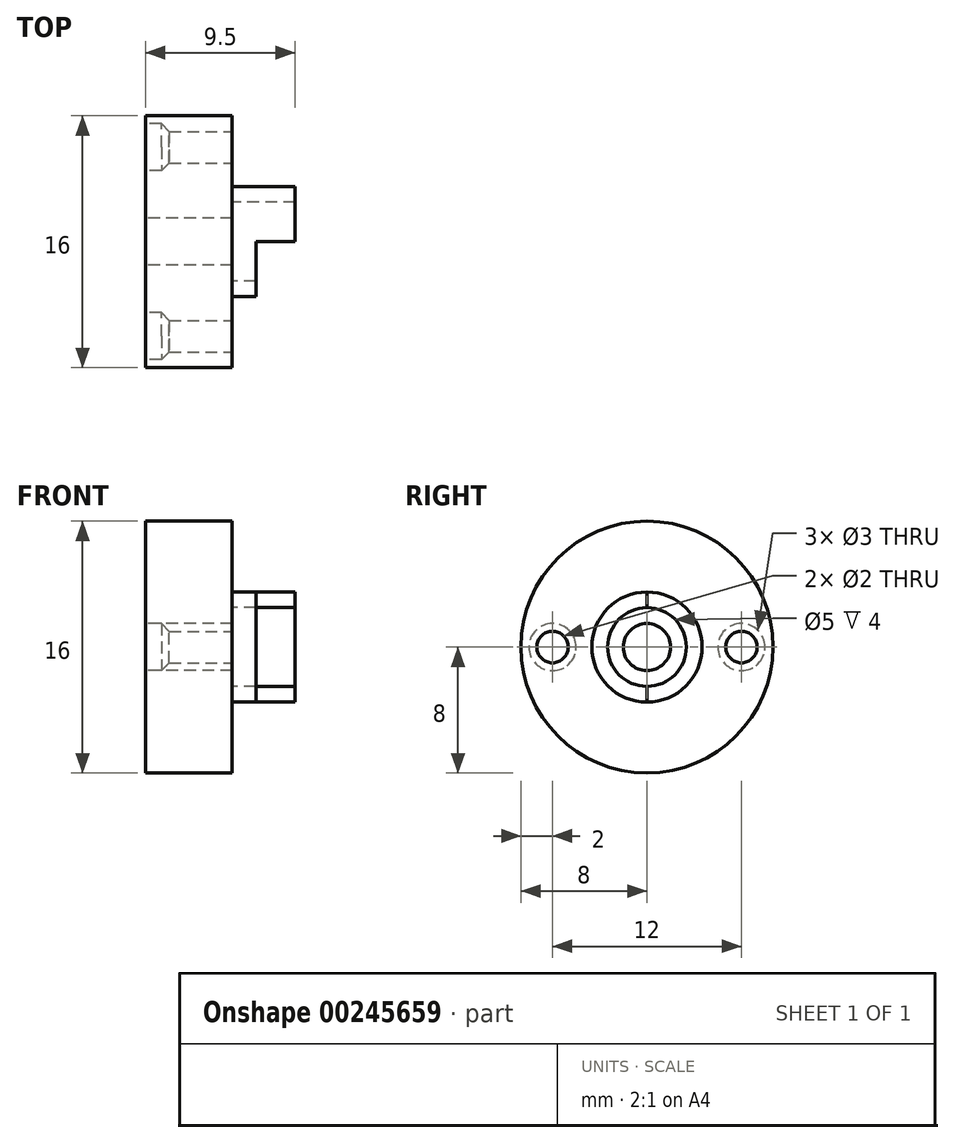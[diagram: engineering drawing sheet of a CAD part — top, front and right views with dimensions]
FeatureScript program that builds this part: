
annotation { "Feature Type Name" : "Feature", "Feature Type Description" : "" }
export const myFeature = defineFeature(function(context is Context, id is Id, definition is map)
    precondition{}
    {
        {
            var Q0;
            Q0=qCreatedBy(makeId("Right.planeOp"),FACE);
            var sketch = newSketch(context, id + "F0", { "sketchPlane" : qUnion([Q0])});
            skCircle(sketch, "E0", {"center": v(0, 0) * mm, "radius": 8 * mm});
            skSolve(sketch);
        }
        {
            var Q0;
            Q0=makeQuery(id+"F0.imprint","IMPRINT",FACE,{"disambiguationData":[TD([[makeQuery(id+"F0.imprint","IMPRINT",EDGE,{"derivedFrom":sQuery(id+"F0.wireOp",EDGE,"E0")}),1.0]])]});
            extrude(context, id + "F1", {"entities" : qUnion([Q0]), "depth" : 5.5 * mm});
        }
        {
            var Q0;
            Q0=makeQuery(id+"F1.opExtrude","CAP_FACE",FACE,{"disambiguationData":[OSD([sQuery(id+"F0.wireOp",EDGE,"E0")])],"isStart":false});
            var sketch = newSketch(context, id + "F2", { "sketchPlane" : qUnion([Q0])});
            skCircle(sketch, "E1", {"center": v(0, 0) * mm, "radius": 3.5 * mm});
            skSolve(sketch);
        }
        {
            var Q0;
            Q0=makeQuery(id+"F2.imprint","IMPRINT",FACE,{"disambiguationData":[TD([[makeQuery(id+"F2.imprint","IMPRINT",EDGE,{"derivedFrom":sQuery(id+"F2.wireOp",EDGE,"E1")}),1.0]])]});
            extrude(context, id + "F3", {"entities" : qUnion([Q0]), "operationType" : NewBodyOperationType.ADD, "depth" : 1.5 * mm});
        }
        {
            var Q0;
            Q0=makeQuery(id+"F3.opExtrude","CAP_FACE",FACE,{"disambiguationData":[OSD([sQuery(id+"F2.wireOp",EDGE,"E1")])],"isStart":false});
            var sketch = newSketch(context, id + "F4", { "sketchPlane" : qUnion([Q0])});
            skArc(sketch, "E2", {"start": v(0, -3.5) * mm, "mid": v(3.51, 0) * mm, "end": v(0, 3.5) * mm});
            skArc(sketch, "E3", {"start": v(0, -2.5) * mm, "mid": v(2.5, 0) * mm, "end": v(0, 2.5) * mm});
            skLineSegment(sketch, "E4", {"start": v(0, 3.5) * mm, "end": v(0, 2.5) * mm});
            skLineSegment(sketch, "E5", {"start": v(0, -3.5) * mm, "end": v(0, -2.5) * mm});
            skSolve(sketch);
        }
        {
            var Q0;
            Q0=makeQuery(id+"F4.imprint","IMPRINT",FACE,{"disambiguationData":[TD([[makeQuery(id+"F4.imprint","IMPRINT",EDGE,{"derivedFrom":sQuery(id+"F4.wireOp",EDGE,"E3")}),-1.0]])]});
            extrude(context, id + "F5", {"entities" : qUnion([Q0]), "operationType" : NewBodyOperationType.ADD, "depth" : 2.5 * mm});
        }
        {
            var Q0;
            Q0=makeQuery(id+"F3.opExtrude","CAP_FACE",FACE,{"disambiguationData":[OSD([sQuery(id+"F2.wireOp",EDGE,"E1")])],"isStart":false});
            var sketch = newSketch(context, id + "F6", { "sketchPlane" : qUnion([Q0])});
            skCircle(sketch, "E6", {"center": v(0, 0) * mm, "radius": 2.5 * mm});
            skSolve(sketch);
        }
        {
            var Q0;
            {var subQ0=sQuery(id+"F6.wireOp",EDGE,"E6");var subQ1=makeQuery(id+"F6.imprint","INTERSECT",VERTEX,{"derivedFrom":[makeQuery(id+"F5.opExtrude","CAP_EDGE",EDGE,{"disambiguationData":[OSD([sQuery(id+"F4.wireOp",EDGE,"E5")])],"isStart":true}),subQ0]});Q0=makeQuery(id+"F6.imprint","IMPRINT",FACE,{"disambiguationData":[TD([[makeQuery(id+"F6.imprint","IMPRINT",EDGE,{"disambiguationData":[TD([[subQ1,-1.0]])],"derivedFrom":subQ0}),1.0]])]});}
            extrude(context, id + "F7", {"entities" : qUnion([Q0]), "operationType" : NewBodyOperationType.REMOVE, "oppositeDirection" : true, "depth" : 1.5 * mm});
        }
        {
            var Q0;
            Q0=makeQuery(id+"F7.boolean.opBoolean","COPY",FACE,{"derivedFrom":makeQuery(id+"F7.opExtrude","CAP_FACE",FACE,{"disambiguationData":[OSD([sQuery(id+"F6.wireOp",EDGE,"E6")])],"isStart":false})});
            var sketch = newSketch(context, id + "F8", { "sketchPlane" : qUnion([Q0])});
            skPoint(sketch, "E7", {"position": v(0, 0) * mm});
            skSolve(sketch);
        }
        {
            var Q0;
            Q0=sQuery(id+"F8.wireOp",VERTEX,"E7");
            var Q1;
            Q1=makeQuery(id+"F1.opExtrude","SWEPT_BODY",BODY,{"disambiguationData":[OSD([sQuery(id+"F0.wireOp",EDGE,"E0")])]});
            hole(context, id + "F9", {"style" : HoleStyle.SIMPLE, "endStyle" : HoleEndStyle.THROUGH, "holeDiameter" : 3 * mm, "tappedDepth" : 15 * mm, "tapClearance" : 0, "locations" : qUnion([Q0]), "scope" : qUnion([Q1]), "startStyle" : HoleStartStyle.SKETCH});
        }
        {
            var Q0;
            Q0=makeQuery(id+"F1.opExtrude","CAP_FACE",FACE,{"disambiguationData":[OSD([sQuery(id+"F0.wireOp",EDGE,"E0")])],"isStart":true});
            var sketch = newSketch(context, id + "F10", { "sketchPlane" : qUnion([Q0])});
            skCircle(sketch, "E8", {"center": v(-6, 0) * mm, "radius": 1.5 * mm});
            skCircle(sketch, "E9", {"center": v(6, 0) * mm, "radius": 1.5 * mm});
            skSolve(sketch);
        }
        {
            var Q0;
            Q0=makeQuery(id+"F10.imprint","IMPRINT",FACE,{"disambiguationData":[TD([[makeQuery(id+"F10.imprint","IMPRINT",EDGE,{"derivedFrom":sQuery(id+"F10.wireOp",EDGE,"E8")}),1.0]])]});
            var Q1;
            Q1=makeQuery(id+"F10.imprint","IMPRINT",FACE,{"disambiguationData":[TD([[makeQuery(id+"F10.imprint","IMPRINT",EDGE,{"derivedFrom":sQuery(id+"F10.wireOp",EDGE,"E9")}),1.0]])]});
            extrude(context, id + "F11", {"entities" : qUnion([Q0, Q1]), "operationType" : NewBodyOperationType.REMOVE, "oppositeDirection" : true, "depth" : 1 * mm});
        }
        {
            var Q0;
            Q0=makeQuery(id+"F11.boolean.opBoolean","COPY",FACE,{"derivedFrom":makeQuery(id+"F11.opExtrude","CAP_FACE",FACE,{"disambiguationData":[OSD([sQuery(id+"F10.wireOp",EDGE,"E8")])],"isStart":false})});
            var sketch = newSketch(context, id + "F12", { "sketchPlane" : qUnion([Q0])});
            skPoint(sketch, "E10", {"position": v(-6, 0) * mm});
            skPoint(sketch, "E11", {"position": v(6, 0) * mm});
            skSolve(sketch);
        }
        {
            var Q0;
            Q0=sQuery(id+"F12.wireOp",VERTEX,"E10");
            var Q1;
            Q1=sQuery(id+"F12.wireOp",VERTEX,"E11");
            var Q2;
            Q2=makeQuery(id+"F1.opExtrude","SWEPT_BODY",BODY,{"disambiguationData":[OSD([sQuery(id+"F0.wireOp",EDGE,"E0")])]});
            hole(context, id + "F13", {"style" : HoleStyle.C_SINK, "endStyle" : HoleEndStyle.THROUGH, "holeDiameter" : 2 * mm, "cSinkDiameter" : 3 * mm, "cSinkAngle" : 90 * degree, "tappedDepth" : 15 * mm, "tapClearance" : 0, "locations" : qUnion([Q0, Q1]), "scope" : qUnion([Q2]), "startStyle" : HoleStartStyle.SKETCH});
        }
    });
